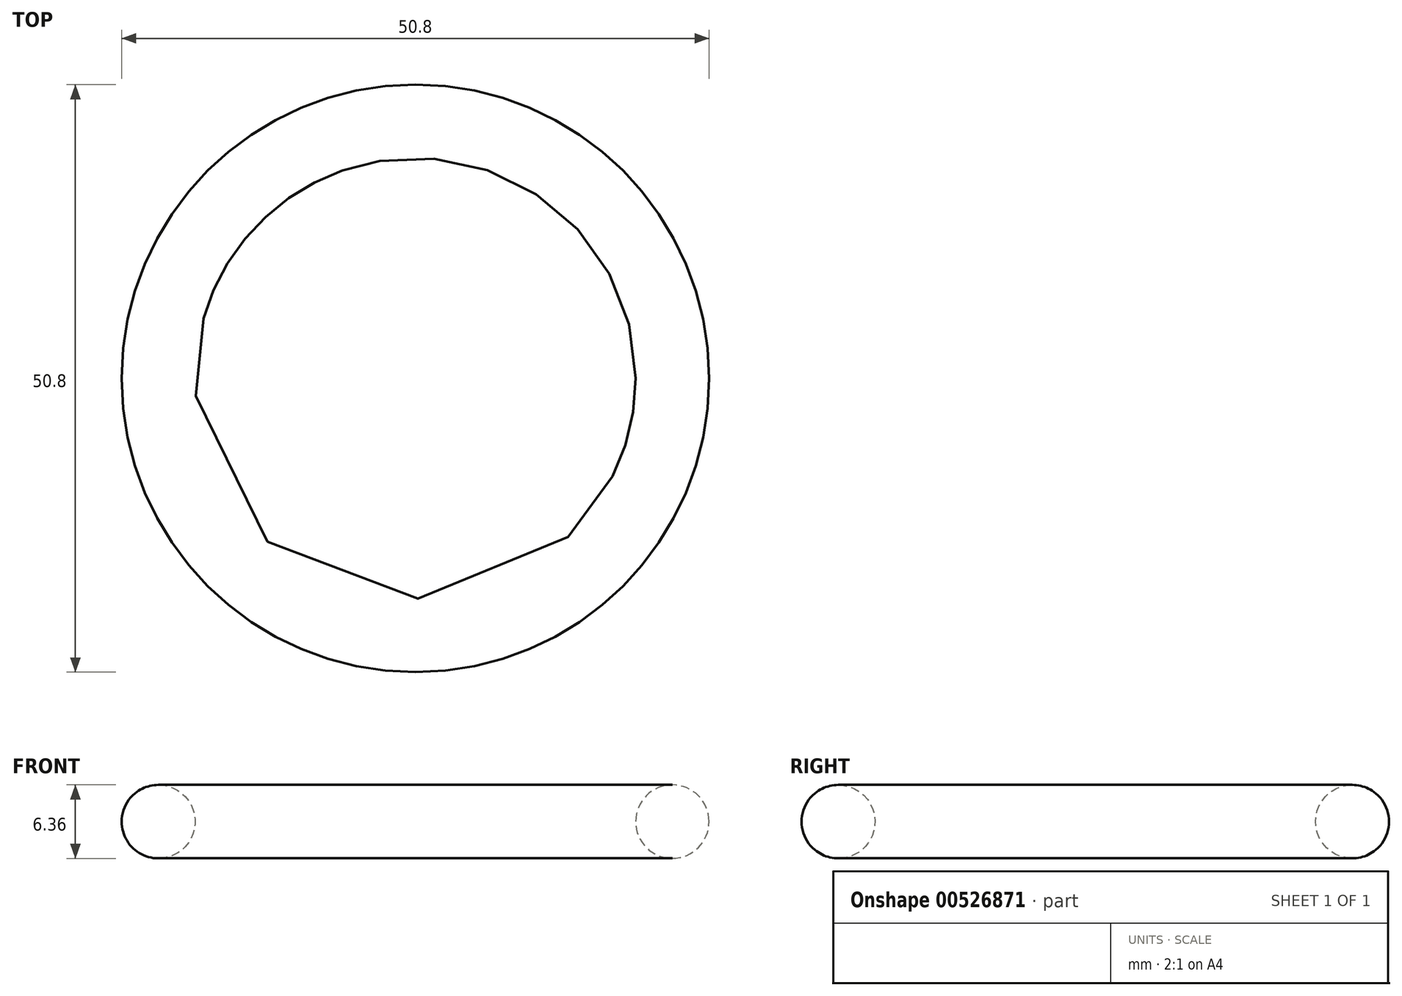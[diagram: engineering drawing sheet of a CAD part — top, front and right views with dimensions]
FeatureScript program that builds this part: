
annotation { "Feature Type Name" : "Feature", "Feature Type Description" : "" }
export const myFeature = defineFeature(function(context is Context, id is Id, definition is map)
    precondition{}
    {
        {
            var Q0;
            Q0=qCreatedBy(makeId("Front.planeOp"),FACE);
            var sketch = newSketch(context, id + "F0", { "sketchPlane" : qUnion([Q0])});
            skCircle(sketch, "E0", {"center": v(-22.23, 0) * mm, "radius": 3.18 * mm});
            skLineSegment(sketch, "E1", {"start": v(0, 10.7) * mm, "end": v(0, -11.68) * mm, "construction": true});
            skSolve(sketch);
        }
        {
            var Q0;
            Q0 = qSketchRegion(id + "F0", true);
            var Q1;
            Q1=sQuery(id+"F0.wireOp",EDGE,"E1");
            revolve(context, id + "F1", {"entities" : qUnion([Q0]), "axis" : qUnion([Q1]), "revolveType" : RevolveType.FULL});
        }
    });
